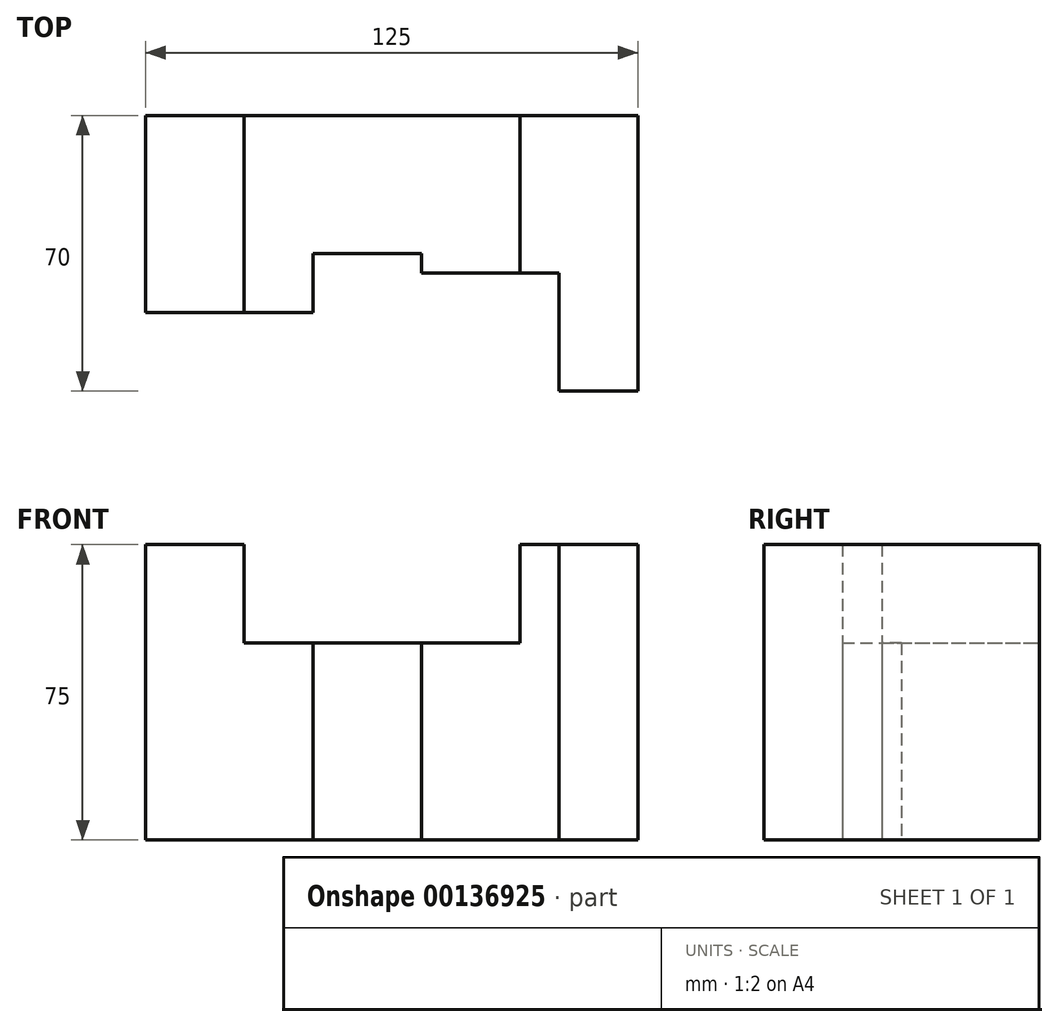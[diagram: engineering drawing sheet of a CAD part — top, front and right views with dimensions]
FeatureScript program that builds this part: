
annotation { "Feature Type Name" : "Feature", "Feature Type Description" : "" }
export const myFeature = defineFeature(function(context is Context, id is Id, definition is map)
    precondition{}
    {
        {
            var Q0;
            Q0=qCreatedBy(makeId("Top.planeOp"),FACE);
            var sketch = newSketch(context, id + "F0", { "sketchPlane" : qUnion([Q0])});
            skLineSegment(sketch, "E0", {"start": v(0, 0) * mm, "end": v(0, 70) * mm});
            skLineSegment(sketch, "E1", {"start": v(0, 70) * mm, "end": v(-125, 70) * mm});
            skLineSegment(sketch, "E2", {"start": v(-125, 70) * mm, "end": v(-125, 20) * mm});
            skLineSegment(sketch, "E3", {"start": v(-125, 20) * mm, "end": v(-82.5, 20) * mm});
            skLineSegment(sketch, "E4", {"start": v(-82.5, 20) * mm, "end": v(-82.5, 35) * mm});
            skLineSegment(sketch, "E5", {"start": v(-82.5, 35) * mm, "end": v(-55, 35) * mm});
            skLineSegment(sketch, "E6", {"start": v(-55, 35) * mm, "end": v(-55, 30) * mm});
            skLineSegment(sketch, "E7", {"start": v(-55, 30) * mm, "end": v(-20, 30) * mm});
            skLineSegment(sketch, "E8", {"start": v(-20, 30) * mm, "end": v(-20, 0) * mm});
            skLineSegment(sketch, "E9", {"start": v(-20, 0) * mm, "end": v(0, 0) * mm});
            skSolve(sketch);
        }
        {
            var Q0;
            Q0 = qSketchRegion(id + "F0", true);
            extrude(context, id + "F1", {"entities" : qUnion([Q0]), "depth" : 50 * mm});
        }
        {
            var Q0;
            Q0=makeQuery(id+"F1.opExtrude","CAP_FACE",FACE,{"disambiguationData":[OSD([sQuery(id+"F0.wireOp",EDGE,"E0"),sQuery(id+"F0.wireOp",EDGE,"E1"),sQuery(id+"F0.wireOp",EDGE,"E2"),sQuery(id+"F0.wireOp",EDGE,"E3"),sQuery(id+"F0.wireOp",EDGE,"E4"),sQuery(id+"F0.wireOp",EDGE,"E5"),sQuery(id+"F0.wireOp",EDGE,"E6"),sQuery(id+"F0.wireOp",EDGE,"E7"),sQuery(id+"F0.wireOp",EDGE,"E8"),sQuery(id+"F0.wireOp",EDGE,"E9")])],"isStart":false});
            var sketch = newSketch(context, id + "F2", { "sketchPlane" : qUnion([Q0])});
            skLineSegment(sketch, "E10", {"start": v(-100, 20) * mm, "end": v(-100, 70) * mm});
            skLineSegment(sketch, "E11", {"start": v(-100, 70) * mm, "end": v(-125, 70) * mm});
            skLineSegment(sketch, "E12", {"start": v(-125, 70) * mm, "end": v(-125, 20) * mm});
            skLineSegment(sketch, "E13", {"start": v(-125, 20) * mm, "end": v(-100, 20) * mm});
            skSolve(sketch);
        }
        {
            var Q0;
            Q0 = qSketchRegion(id + "F2", true);
            extrude(context, id + "F3", {"entities" : qUnion([Q0]), "operationType" : NewBodyOperationType.ADD, "depth" : 25 * mm});
        }
        {
            var Q0;
            Q0=makeQuery(id+"F1.opExtrude","CAP_FACE",FACE,{"disambiguationData":[OSD([sQuery(id+"F0.wireOp",EDGE,"E0"),sQuery(id+"F0.wireOp",EDGE,"E1"),sQuery(id+"F0.wireOp",EDGE,"E2"),sQuery(id+"F0.wireOp",EDGE,"E3"),sQuery(id+"F0.wireOp",EDGE,"E4"),sQuery(id+"F0.wireOp",EDGE,"E5"),sQuery(id+"F0.wireOp",EDGE,"E6"),sQuery(id+"F0.wireOp",EDGE,"E7"),sQuery(id+"F0.wireOp",EDGE,"E8"),sQuery(id+"F0.wireOp",EDGE,"E9")])],"isStart":false});
            var sketch = newSketch(context, id + "F4", { "sketchPlane" : qUnion([Q0])});
            skLineSegment(sketch, "E14", {"start": v(-30, 30) * mm, "end": v(-30, 70) * mm});
            skLineSegment(sketch, "E15", {"start": v(-30, 70) * mm, "end": v(0, 70) * mm});
            skLineSegment(sketch, "E16", {"start": v(0, 70) * mm, "end": v(0, 0) * mm});
            skLineSegment(sketch, "E17", {"start": v(0, 0) * mm, "end": v(-20, 0) * mm});
            skLineSegment(sketch, "E18", {"start": v(-20, 0) * mm, "end": v(-20, 30) * mm});
            skLineSegment(sketch, "E19", {"start": v(-20, 30) * mm, "end": v(-30, 30) * mm});
            skSolve(sketch);
        }
        {
            var Q0;
            Q0 = qSketchRegion(id + "F4", true);
            extrude(context, id + "F5", {"entities" : qUnion([Q0]), "operationType" : NewBodyOperationType.ADD, "depth" : 25 * mm});
        }
    });
